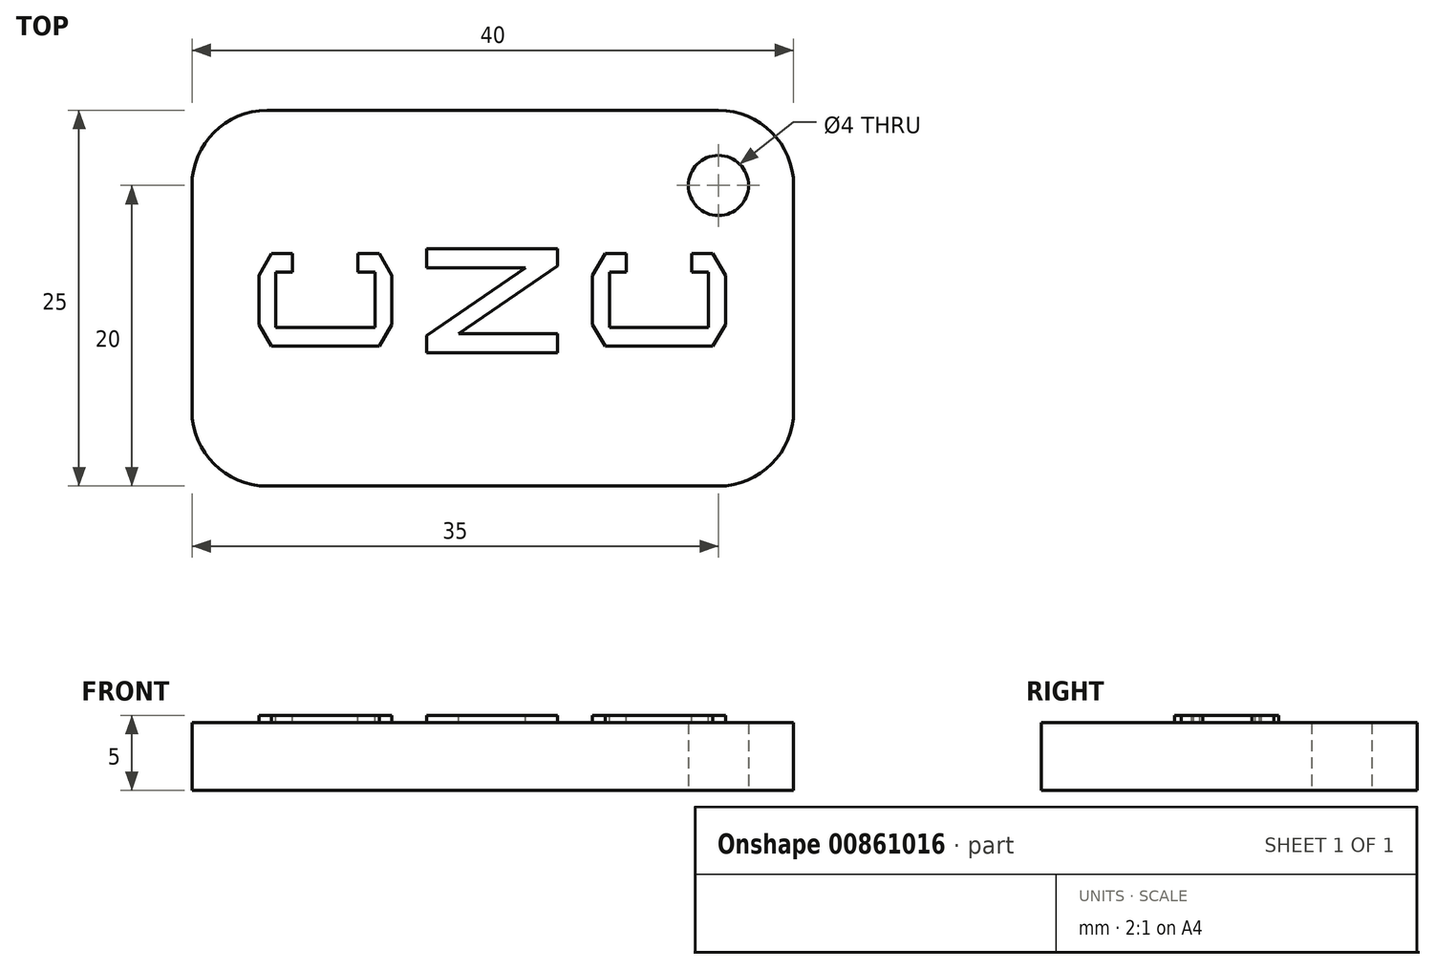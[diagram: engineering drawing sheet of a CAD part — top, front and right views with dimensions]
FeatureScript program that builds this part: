
annotation { "Feature Type Name" : "Feature", "Feature Type Description" : "" }
export const myFeature = defineFeature(function(context is Context, id is Id, definition is map)
    precondition{}
    {
        {
            var Q0;
            Q0=qCreatedBy(makeId("Top.planeOp"),FACE);
            var sketch = newSketch(context, id + "F0", { "sketchPlane" : qUnion([Q0])});
            skLineSegment(sketch, "E0.bottom", {"start": v(-15, 12.5) * mm, "end": v(15, 12.5) * mm});
            skLineSegment(sketch, "E0.top", {"start": v(-15, -12.5) * mm, "end": v(15, -12.5) * mm});
            skLineSegment(sketch, "E0.left", {"start": v(-20, 7.5) * mm, "end": v(-20, -7.5) * mm});
            skLineSegment(sketch, "E0.right", {"start": v(20, 7.5) * mm, "end": v(20, -7.5) * mm});
            skPoint(sketch, "E0.middle", {"position": v(0, 0) * mm});
            skPoint(sketch, "E1.visualSharp", {"position": v(-20, 12.5) * mm});
            skArc(sketch, "E1.filletArc", {"start": v(-15, 12.5) * mm, "mid": v(-18.54, 11.04) * mm, "end": v(-20, 7.5) * mm});
            skPoint(sketch, "E2.visualSharp", {"position": v(-20, -12.5) * mm});
            skArc(sketch, "E2.filletArc", {"start": v(-20, -7.5) * mm, "mid": v(-18.54, -11.04) * mm, "end": v(-15, -12.5) * mm});
            skPoint(sketch, "E3.visualSharp", {"position": v(20, -12.5) * mm});
            skArc(sketch, "E3.filletArc", {"start": v(15, -12.5) * mm, "mid": v(18.54, -11.04) * mm, "end": v(20, -7.5) * mm});
            skPoint(sketch, "E4.visualSharp", {"position": v(20, 12.5) * mm});
            skArc(sketch, "E4.filletArc", {"start": v(20, 7.5) * mm, "mid": v(18.54, 11.04) * mm, "end": v(15, 12.5) * mm});
            skCircle(sketch, "E5", {"center": v(15, 7.5) * mm, "radius": 2 * mm});
            skSolve(sketch);
        }
        {
            var Q0;
            Q0=makeQuery(id+"F0.imprint","IMPRINT",FACE,{"disambiguationData":[TD([[makeQuery(id+"F0.imprint","IMPRINT",EDGE,{"derivedFrom":sQuery(id+"F0.wireOp",EDGE,"E0.bottom")}),-1.0]])]});
            extrude(context, id + "F1", {"entities" : qUnion([Q0]), "depth" : 5 * mm, "offsetDistance" : 25 * mm});
        }
        {
            var Q0;
            Q0=makeQuery(id+"F1.opExtrude","CAP_FACE",FACE,{"disambiguationData":[OSD([sQuery(id+"F0.wireOp",EDGE,"E0.bottom"),sQuery(id+"F0.wireOp",EDGE,"E0.top"),sQuery(id+"F0.wireOp",EDGE,"E0.left"),sQuery(id+"F0.wireOp",EDGE,"E0.right"),sQuery(id+"F0.wireOp",EDGE,"E1.filletArc"),sQuery(id+"F0.wireOp",EDGE,"E2.filletArc"),sQuery(id+"F0.wireOp",EDGE,"E3.filletArc"),sQuery(id+"F0.wireOp",EDGE,"E4.filletArc"),sQuery(id+"F0.wireOp",EDGE,"E5")])],"isStart":false});
            var sketch = newSketch(context, id + "F2", { "sketchPlane" : qUnion([Q0])});
            skLineSegment(sketch, "E6", {"start": v(-8.96, 1.72) * mm, "end": v(-8.96, 2.97) * mm});
            skLineSegment(sketch, "E7", {"start": v(-8.96, 2.97) * mm, "end": v(-7.55, 2.97) * mm});
            skLineSegment(sketch, "E8", {"start": v(-7.55, 2.97) * mm, "end": v(-6.72, 1.52) * mm});
            skLineSegment(sketch, "E9", {"start": v(-6.72, 1.52) * mm, "end": v(-6.72, -1.75) * mm});
            skLineSegment(sketch, "E10", {"start": v(-6.72, -1.75) * mm, "end": v(-7.55, -3.19) * mm});
            skLineSegment(sketch, "E11", {"start": v(-7.55, -3.19) * mm, "end": v(-14.72, -3.19) * mm});
            skLineSegment(sketch, "E12", {"start": v(-14.72, -3.19) * mm, "end": v(-15.55, -1.75) * mm});
            skLineSegment(sketch, "E13", {"start": v(-15.55, -1.75) * mm, "end": v(-15.55, 1.52) * mm});
            skLineSegment(sketch, "E14", {"start": v(-15.55, 1.52) * mm, "end": v(-14.72, 2.97) * mm});
            skLineSegment(sketch, "E15", {"start": v(-14.72, 2.97) * mm, "end": v(-13.31, 2.97) * mm});
            skLineSegment(sketch, "E16", {"start": v(-13.31, 2.97) * mm, "end": v(-13.31, 1.72) * mm});
            skLineSegment(sketch, "E17", {"start": v(-13.31, 1.72) * mm, "end": v(-14.43, 1.72) * mm});
            skLineSegment(sketch, "E18", {"start": v(-14.43, 1.72) * mm, "end": v(-14.43, -1.94) * mm});
            skLineSegment(sketch, "E19", {"start": v(-14.43, -1.94) * mm, "end": v(-7.84, -1.94) * mm});
            skLineSegment(sketch, "E20", {"start": v(-7.84, -1.94) * mm, "end": v(-7.84, 1.72) * mm});
            skLineSegment(sketch, "E21", {"start": v(-7.84, 1.72) * mm, "end": v(-8.96, 1.72) * mm});
            skLineSegment(sketch, "E22", {"start": v(-2.27, -2.38) * mm, "end": v(4.3, -2.38) * mm});
            skLineSegment(sketch, "E23", {"start": v(4.3, -2.38) * mm, "end": v(4.3, -3.62) * mm});
            skLineSegment(sketch, "E24", {"start": v(4.3, -3.62) * mm, "end": v(-4.4, -3.62) * mm});
            skLineSegment(sketch, "E25", {"start": v(-4.4, -3.62) * mm, "end": v(-4.4, -2.5) * mm});
            skLineSegment(sketch, "E26", {"start": v(-4.4, -2.5) * mm, "end": v(2.18, 2.01) * mm});
            skLineSegment(sketch, "E27", {"start": v(2.18, 2.01) * mm, "end": v(2.18, 2.04) * mm});
            skLineSegment(sketch, "E28", {"start": v(2.18, 2.04) * mm, "end": v(-4.4, 2.04) * mm});
            skLineSegment(sketch, "E29", {"start": v(-4.4, 2.04) * mm, "end": v(-4.4, 3.28) * mm});
            skLineSegment(sketch, "E30", {"start": v(-4.4, 3.28) * mm, "end": v(4.3, 3.28) * mm});
            skLineSegment(sketch, "E31", {"start": v(4.3, 3.28) * mm, "end": v(4.3, 2.15) * mm});
            skLineSegment(sketch, "E32", {"start": v(4.3, 2.15) * mm, "end": v(-2.27, -2.35) * mm});
            skLineSegment(sketch, "E33", {"start": v(-2.27, -2.35) * mm, "end": v(-2.27, -2.38) * mm});
            skLineSegment(sketch, "E34", {"start": v(13.23, 1.72) * mm, "end": v(13.23, 2.97) * mm});
            skLineSegment(sketch, "E35", {"start": v(13.23, 2.97) * mm, "end": v(14.63, 2.97) * mm});
            skLineSegment(sketch, "E36", {"start": v(14.63, 2.97) * mm, "end": v(15.46, 1.52) * mm});
            skLineSegment(sketch, "E37", {"start": v(15.46, 1.52) * mm, "end": v(15.46, -1.75) * mm});
            skLineSegment(sketch, "E38", {"start": v(15.46, -1.75) * mm, "end": v(14.63, -3.19) * mm});
            skLineSegment(sketch, "E39", {"start": v(14.63, -3.19) * mm, "end": v(7.47, -3.19) * mm});
            skLineSegment(sketch, "E40", {"start": v(7.47, -3.19) * mm, "end": v(6.63, -1.75) * mm});
            skLineSegment(sketch, "E41", {"start": v(6.63, -1.75) * mm, "end": v(6.63, 1.52) * mm});
            skLineSegment(sketch, "E42", {"start": v(6.63, 1.52) * mm, "end": v(7.47, 2.97) * mm});
            skLineSegment(sketch, "E43", {"start": v(7.47, 2.97) * mm, "end": v(8.87, 2.97) * mm});
            skLineSegment(sketch, "E44", {"start": v(8.87, 2.97) * mm, "end": v(8.87, 1.72) * mm});
            skLineSegment(sketch, "E45", {"start": v(8.87, 1.72) * mm, "end": v(7.75, 1.72) * mm});
            skLineSegment(sketch, "E46", {"start": v(7.75, 1.72) * mm, "end": v(7.75, -1.94) * mm});
            skLineSegment(sketch, "E47", {"start": v(7.75, -1.94) * mm, "end": v(14.34, -1.94) * mm});
            skLineSegment(sketch, "E48", {"start": v(14.34, -1.94) * mm, "end": v(14.34, 1.72) * mm});
            skLineSegment(sketch, "E49", {"start": v(14.34, 1.72) * mm, "end": v(13.23, 1.72) * mm});
            skLineSegment(sketch, "E50.bottom", {"start": v(-21.27, 13.37) * mm, "end": v(21.27, 13.37) * mm});
            skLineSegment(sketch, "E50.top", {"start": v(-21.27, -13.37) * mm, "end": v(21.27, -13.37) * mm});
            skLineSegment(sketch, "E50.left", {"start": v(-21.27, 13.37) * mm, "end": v(-21.27, -13.37) * mm});
            skLineSegment(sketch, "E50.right", {"start": v(21.27, 13.37) * mm, "end": v(21.27, -13.37) * mm});
            skPoint(sketch, "E50.middle", {"position": v(0, 0) * mm});
            skSolve(sketch);
        }
        {
            var Q0;
            Q0=makeQuery(id+"F2.imprint","IMPRINT",FACE,{"disambiguationData":[TD([[makeQuery(id+"F2.imprint","IMPRINT",EDGE,{"derivedFrom":sQuery(id+"F2.wireOp",EDGE,"E50.bottom")}),-1.0]])]});
            var Q1;
            Q1=makeQuery(id+"F2.imprint","IMPRINT",FACE,{"disambiguationData":[TD([[makeQuery(id+"F2.imprint","IMPRINT",EDGE,{"derivedFrom":makeQuery(id+"F1.opExtrude","CAP_EDGE",EDGE,{"disambiguationData":[OSD([sQuery(id+"F0.wireOp",EDGE,"E5")])],"isStart":false})}),1.0]])]});
            var Q2;
            Q2=makeQuery(id+"F2.imprint","IMPRINT",FACE,{"disambiguationData":[TD([[makeQuery(id+"F2.imprint","IMPRINT",EDGE,{"derivedFrom":sQuery(id+"F2.wireOp",EDGE,"E6")}),1.0]])]});
            extrude(context, id + "F3", {"entities" : qUnion([Q0, Q1, Q2]), "operationType" : NewBodyOperationType.REMOVE, "oppositeDirection" : true, "depth" : 0.5 * mm, "offsetDistance" : 25 * mm});
        }
    });
